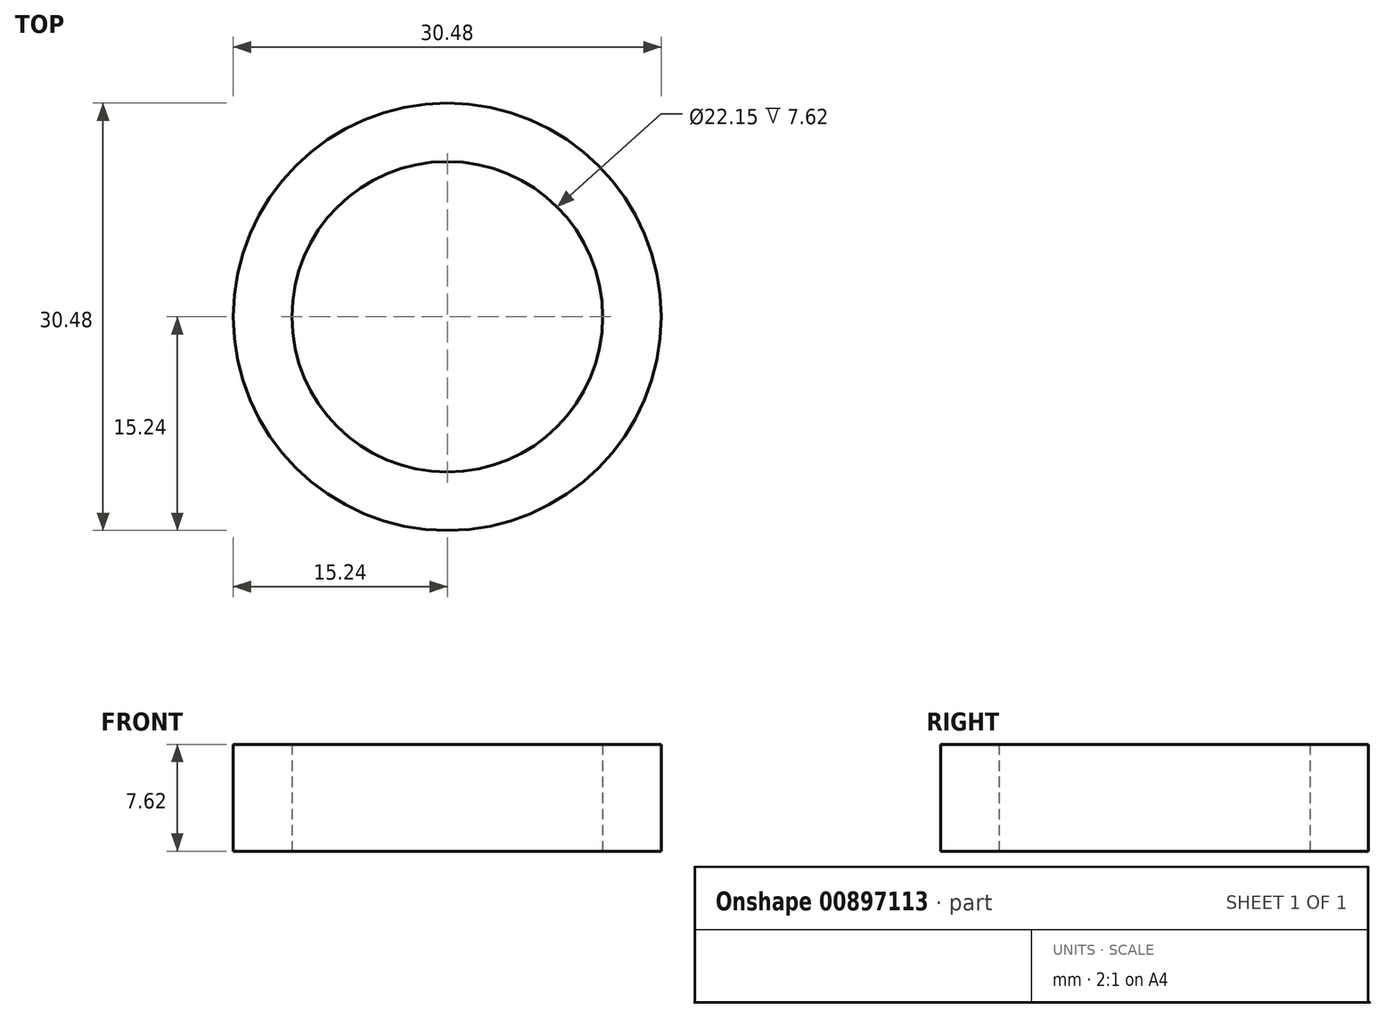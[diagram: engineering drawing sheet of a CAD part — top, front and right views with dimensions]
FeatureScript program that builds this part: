
annotation { "Feature Type Name" : "Feature", "Feature Type Description" : "" }
export const myFeature = defineFeature(function(context is Context, id is Id, definition is map)
    precondition{}
    {
        {
            var Q0;
            Q0=qCreatedBy(makeId("Top.planeOp"),FACE);
            var sketch = newSketch(context, id + "F0", { "sketchPlane" : qUnion([Q0])});
            skCircle(sketch, "E0", {"center": v(0, 0) * mm, "radius": 11.07 * mm});
            skCircle(sketch, "E1", {"center": v(0, 0) * mm, "radius": 15.24 * mm});
            skSolve(sketch);
        }
        {
            var Q0;
            Q0=qSketchRegion(id+"F0",true);
            extrude(context, id + "F1", {"entities" : qUnion([Q0]), "depth" : 7.62 * mm});
        }
    });
